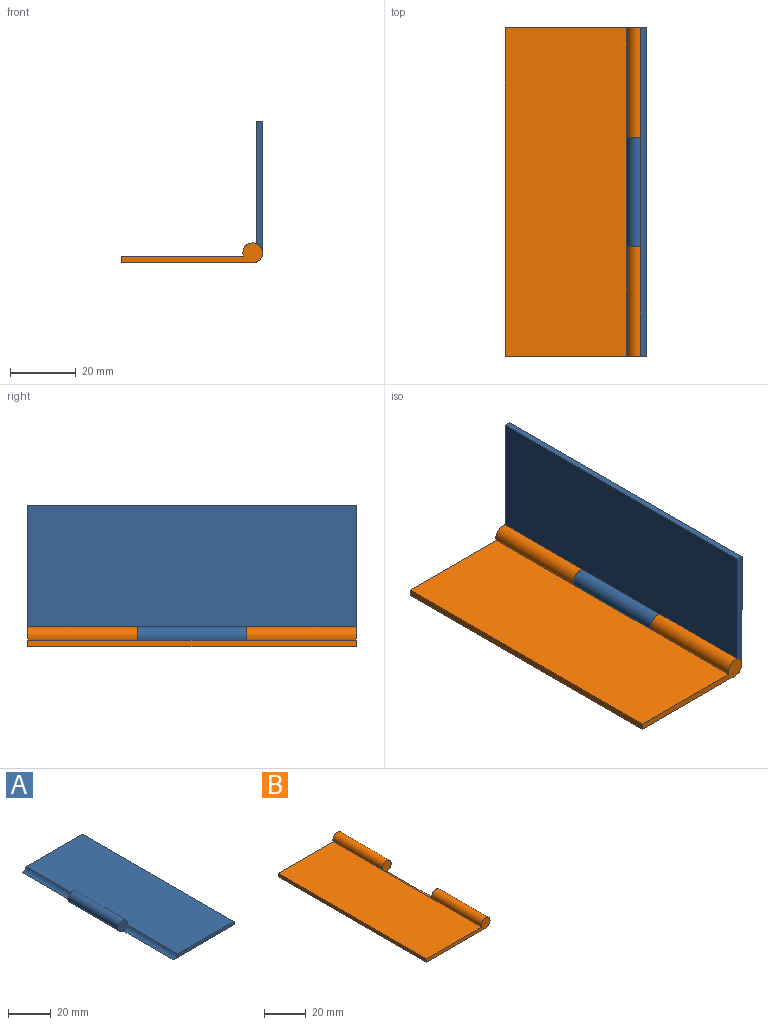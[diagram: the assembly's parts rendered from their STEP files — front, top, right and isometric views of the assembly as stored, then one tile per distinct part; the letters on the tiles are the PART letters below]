
ASSEMBLY  parts=2 mates=1
PART A: 10 faces, bbox 43x100x6 mm
  f0: cylinder r=3mm len=33.33mm, axis (0,1,0), area 505.2mm2, adj f2,f3,f7,f9
  f1: plane 100x2mm, normal (1,0,0), area 200mm2, adj f2,f3,f4,f5
  f2: plane 100x40mm, normal (0,0,-1), area 4000mm2, adj f0,f1,f4,f5,f6,f8
  f3: plane 100x37.17mm, normal (0,0,1), area 3717.2mm2, adj f0,f1,f4,f5,f6,f8
  f4: plane 40x2mm, normal (0,-1,0), area 75.9mm2, adj f1,f2,f3,f8
  f5: plane 40x2mm, normal (0,1,0), area 75.9mm2, adj f1,f2,f3,f6
  f6: cylinder r=3mm len=33.33mm, axis (0,1,0), area 123.1mm2, adj f2,f3,f5,f7
  f7: plane 6x6mm, normal (0,1,0), area 28.3mm2, adj f0,f6
  f8: cylinder r=3mm len=33.33mm, axis (0,1,0), area 123.1mm2, adj f2,f3,f4,f9
  f9: plane 6x6mm, normal (0,-1,0), area 28.3mm2, adj f0,f8
PART B: 10 faces, bbox 43x100x6 mm
  f0: cylinder r=3mm len=33.33mm, axis (0,1,0), area 505.2mm2, adj f2,f4,f6,f8
  f1: plane 100x2mm, normal (-1,0,0), area 200mm2, adj f2,f4,f5,f6
  f2: plane 100x40mm, normal (0,0,-1), area 4000mm2, adj f0,f1,f3,f5,f6,f9
  f3: cylinder r=3mm len=33.33mm, axis (0,1,0), area 505.2mm2, adj f2,f4,f5,f7
  f4: plane 100x37.17mm, normal (0,0,1), area 3717.2mm2, adj f0,f1,f3,f5,f6,f9
  f5: plane 43x6mm, normal (0,-1,0), area 104.1mm2, adj f1,f2,f3,f4
  f6: plane 43x6mm, normal (0,1,0), area 104.1mm2, adj f0,f1,f2,f4
  f7: plane 6x6mm, normal (0,1,0), area 28.3mm2, adj f3,f9
  f8: plane 6x6mm, normal (0,-1,0), area 28.3mm2, adj f0,f9
  f9: cylinder r=3mm len=33.33mm, axis (0,1,0), area 123.1mm2, adj f2,f4,f7,f8
PLACE A rot(axis=(0,-1,0),90deg) t=(2.87,0.53,3.03)mm
PLACE B t=(-0.13,0.53,0.03)mm fixed
MATE revolute B.f0 <-> A.f6  axis (0,1,0) through (-0.13,-66.13,3.03)mm
